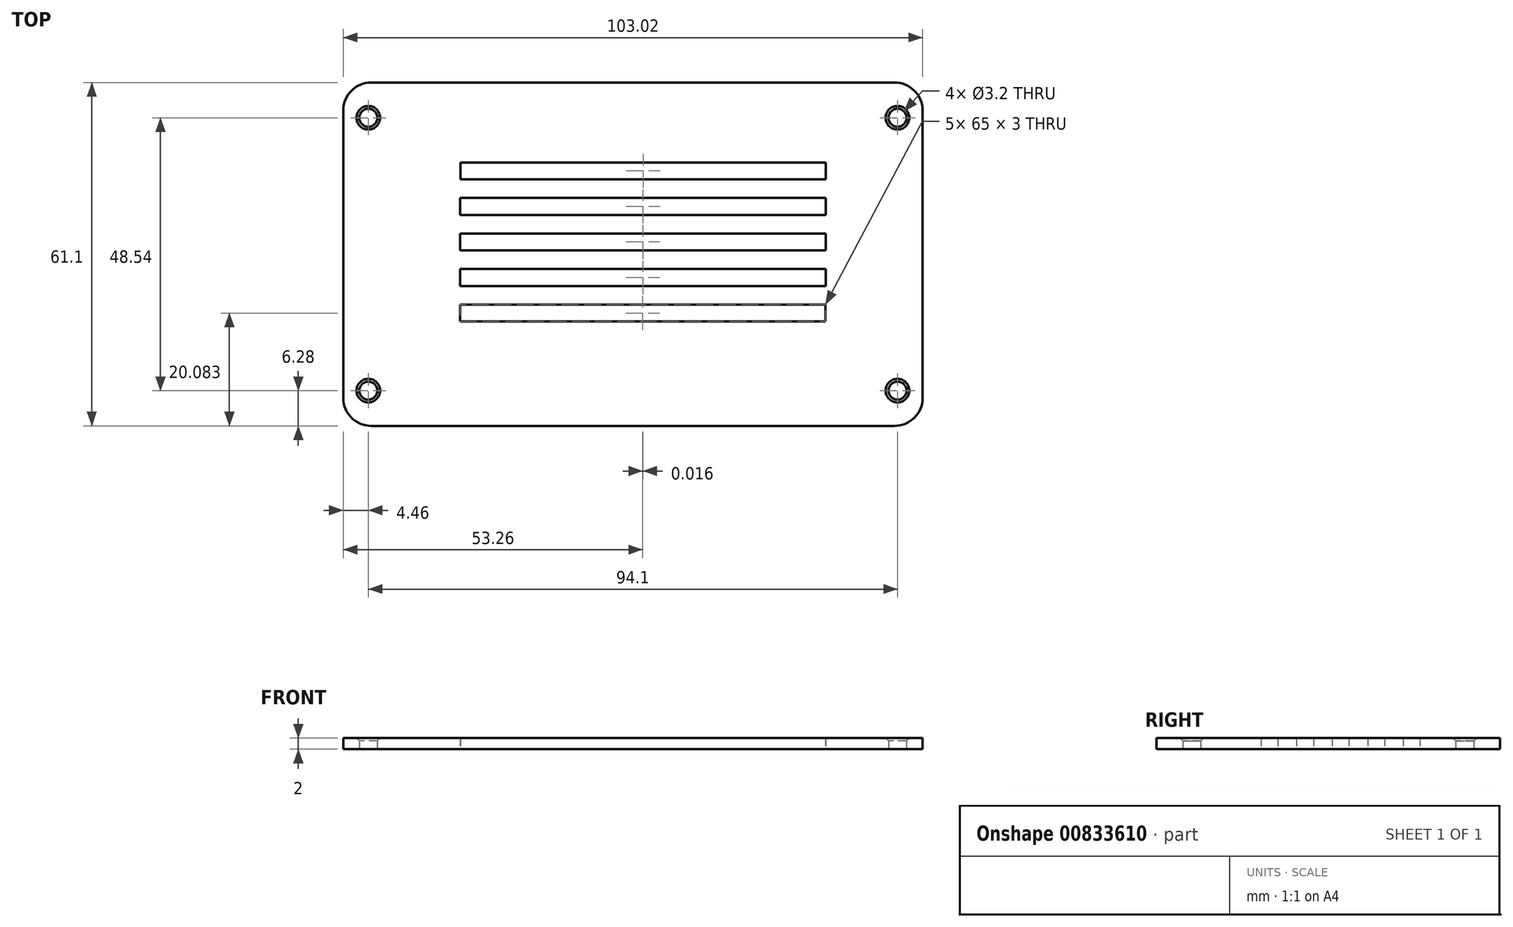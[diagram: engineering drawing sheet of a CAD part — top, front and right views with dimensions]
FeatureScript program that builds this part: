
annotation { "Feature Type Name" : "Feature", "Feature Type Description" : "" }
export const myFeature = defineFeature(function(context is Context, id is Id, definition is map)
    precondition{}
    {
        {
            var Q0;
            Q0=qCreatedBy(makeId("Top.planeOp"),FACE);
            var sketch = newSketch(context, id + "F0", { "sketchPlane" : qUnion([Q0])});
            skPoint(sketch, "E0.middle", {"position": v(0, 0) * mm});
            skLineSegment(sketch, "E1.bottom", {"start": v(45.45, -24.27) * mm, "end": v(42.8, -24.27) * mm});
            skCircle(sketch, "E2", {"center": v(47.05, 24.27) * mm, "radius": 1.6 * mm});
            skCircle(sketch, "E3", {"center": v(47.05, -24.27) * mm, "radius": 1.6 * mm});
            skCircle(sketch, "E4", {"center": v(-47.05, 24.27) * mm, "radius": 1.6 * mm});
            skCircle(sketch, "E5", {"center": v(-47.05, -24.27) * mm, "radius": 1.6 * mm});
            skLineSegment(sketch, "E6.bottom", {"start": v(51.51, 30.55) * mm, "end": v(-51.51, 30.55) * mm});
            skLineSegment(sketch, "E6.top", {"start": v(51.51, -30.55) * mm, "end": v(-51.51, -30.55) * mm});
            skLineSegment(sketch, "E6.left", {"start": v(51.51, 30.55) * mm, "end": v(51.51, -30.55) * mm});
            skLineSegment(sketch, "E6.right", {"start": v(-51.51, 30.55) * mm, "end": v(-51.51, -30.55) * mm});
            skPoint(sketch, "E7.end.orphan", {"position": v(0, 30.55) * mm});
            skPoint(sketch, "E7.start.orphan", {"position": v(0, 27.55) * mm});
            skLineSegment(sketch, "E8.bottom", {"start": v(-30.68, 16.32) * mm, "end": v(34.32, 16.32) * mm});
            skLineSegment(sketch, "E8.top", {"start": v(-30.68, 13.32) * mm, "end": v(34.32, 13.32) * mm});
            skLineSegment(sketch, "E8.left", {"start": v(-30.68, 16.32) * mm, "end": v(-30.68, 13.32) * mm});
            skLineSegment(sketch, "E8.right", {"start": v(34.32, 16.32) * mm, "end": v(34.32, 13.32) * mm});
            skLineSegment(sketch, "E9.0.1.0", {"start": v(-30.7, 7) * mm, "end": v(34.3, 7) * mm});
            skLineSegment(sketch, "E9.0.1.1", {"start": v(-30.7, 10) * mm, "end": v(34.3, 10) * mm});
            skLineSegment(sketch, "E9.0.1.2", {"start": v(34.3, 10) * mm, "end": v(34.3, 7) * mm});
            skLineSegment(sketch, "E9.0.1.3", {"start": v(-30.7, 10) * mm, "end": v(-30.7, 7) * mm});
            skLineSegment(sketch, "E9.0.2.0", {"start": v(-30.72, 0.68) * mm, "end": v(34.28, 0.68) * mm});
            skLineSegment(sketch, "E9.0.2.1", {"start": v(-30.72, 3.68) * mm, "end": v(34.28, 3.68) * mm});
            skLineSegment(sketch, "E9.0.2.2", {"start": v(34.28, 3.68) * mm, "end": v(34.28, 0.68) * mm});
            skLineSegment(sketch, "E9.0.2.3", {"start": v(-30.72, 3.68) * mm, "end": v(-30.72, 0.68) * mm});
            skLineSegment(sketch, "E9.0.3.0", {"start": v(-30.73, -5.64) * mm, "end": v(34.27, -5.64) * mm});
            skLineSegment(sketch, "E9.0.3.1", {"start": v(-30.73, -2.64) * mm, "end": v(34.27, -2.64) * mm});
            skLineSegment(sketch, "E9.0.3.2", {"start": v(34.27, -2.64) * mm, "end": v(34.27, -5.64) * mm});
            skLineSegment(sketch, "E9.0.3.3", {"start": v(-30.73, -2.64) * mm, "end": v(-30.73, -5.64) * mm});
            skLineSegment(sketch, "E9.0.4.0", {"start": v(-30.75, -11.97) * mm, "end": v(34.25, -11.97) * mm});
            skLineSegment(sketch, "E9.0.4.1", {"start": v(-30.75, -8.97) * mm, "end": v(34.25, -8.97) * mm});
            skLineSegment(sketch, "E9.0.4.2", {"start": v(34.25, -8.97) * mm, "end": v(34.25, -11.97) * mm});
            skLineSegment(sketch, "E9.0.4.3", {"start": v(-30.75, -8.97) * mm, "end": v(-30.75, -11.97) * mm});
            skLineSegment(sketch, "E9.direction1", {"start": v(-30.68, 13.32) * mm, "end": v(-5.68, 13.32) * mm, "construction": true});
            skLineSegment(sketch, "E9.direction2", {"start": v(-30.68, 13.32) * mm, "end": v(-30.7, 7) * mm, "construction": true});
            skSolve(sketch);
        }
        {
            var Q0;
            Q0=makeQuery(id+"F0.imprint","IMPRINT",FACE,{"disambiguationData":[TD([[makeQuery(id+"F0.imprint","IMPRINT",EDGE,{"derivedFrom":sQuery(id+"F0.wireOp",EDGE,"E2")}),-1.0]])]});
            extrude(context, id + "F1", {"entities" : qUnion([Q0]), "depth" : 2 * mm, "offsetDistance" : 25 * mm});
        }
        {
            var Q0;
            Q0=makeQuery(id+"F1.opExtrude","SWEPT_EDGE",EDGE,{"disambiguationData":[OSD([sQuery(id+"F0.wireOp",EDGE,"E6.top"),sQuery(id+"F0.wireOp",EDGE,"E6.right")])]});
            var Q1;
            Q1=makeQuery(id+"F1.opExtrude","SWEPT_EDGE",EDGE,{"disambiguationData":[OSD([sQuery(id+"F0.wireOp",EDGE,"E6.bottom"),sQuery(id+"F0.wireOp",EDGE,"E6.right")])]});
            var Q2;
            Q2=makeQuery(id+"F1.opExtrude","SWEPT_EDGE",EDGE,{"disambiguationData":[OSD([sQuery(id+"F0.wireOp",EDGE,"E6.top"),sQuery(id+"F0.wireOp",EDGE,"E6.left")])]});
            var Q3;
            Q3=makeQuery(id+"F1.opExtrude","SWEPT_EDGE",EDGE,{"disambiguationData":[OSD([sQuery(id+"F0.wireOp",EDGE,"E6.bottom"),sQuery(id+"F0.wireOp",EDGE,"E6.left")])]});
            fillet(context, id + "F2", {"entities" : qUnion([Q0, Q1, Q2, Q3]), "radius" : 5 * mm, "tangentPropagation" : true, "allowEdgeOverflow" : false});
        }
        {
            var Q0;
            Q0=makeQuery(id+"F1.opExtrude","CAP_EDGE",EDGE,{"disambiguationData":[OSD([sQuery(id+"F0.wireOp",EDGE,"E5")])],"isStart":false});
            var Q1;
            Q1=makeQuery(id+"F1.opExtrude","CAP_EDGE",EDGE,{"disambiguationData":[OSD([sQuery(id+"F0.wireOp",EDGE,"E4")])],"isStart":false});
            var Q2;
            Q2=makeQuery(id+"F1.opExtrude","CAP_EDGE",EDGE,{"disambiguationData":[OSD([sQuery(id+"F0.wireOp",EDGE,"E2")])],"isStart":false});
            var Q3;
            Q3=makeQuery(id+"F1.opExtrude","CAP_EDGE",EDGE,{"disambiguationData":[OSD([sQuery(id+"F0.wireOp",EDGE,"E3")])],"isStart":false});
            chamfer(context, id + "F3", {"entities" : qUnion([Q0, Q1, Q2, Q3]), "width" : 0.5 * mm, "tangentPropagation" : true});
        }
    });
